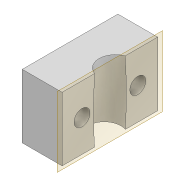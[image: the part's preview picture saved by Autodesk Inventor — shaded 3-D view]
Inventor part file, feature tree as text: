
AUTODESK INVENTOR PART (.ipt)
format: ipt  version: 2022 (Build 260153000, 153)  size: 130,560 bytes
history: native  units: mm
features: extrude x4, sketch x4, plane x1, projected_geometry x1
ambient origin geometry x8: Origin, YZ Plane, XZ Plane, XY Plane, X Axis, Y Axis, Z Axis, Center Point
bodies: Solid1 (feature_tree)
feature tree (10):
  extrude  "Extrusion1"  Depth=5.0mm
  plane  "Work Plane1"
  extrude  "Extrusion2"  Depth=6.0mm
  extrude  "Extrusion3"  Depth=5.0mm
  extrude  "Extrusion4"  Depth=10.0mm
  sketch  "Sketch1"  dims[d0=4.0mm d2=5.0mm]
  sketch  "Sketch4"  dims[d3=6.0mm d4=6.0mm]
  sketch  "Sketch5"  dims[d5=8.0mm d6=0.0mm d7=5.0mm]
  projected_geometry  "Projected Loop1"
  sketch  "Sketch6"  dims[d8=1.745329mm d9=4.1mm d10=100.0mm d11=0.0mm d12=4.2mm d13=2.0mm d14=2.0mm d15=2.5mm d16=2.5mm d17=4.0mm d18=4.0mm d19=100.0mm d20=0.0mm d21=10.0mm d22=0.0mm]
